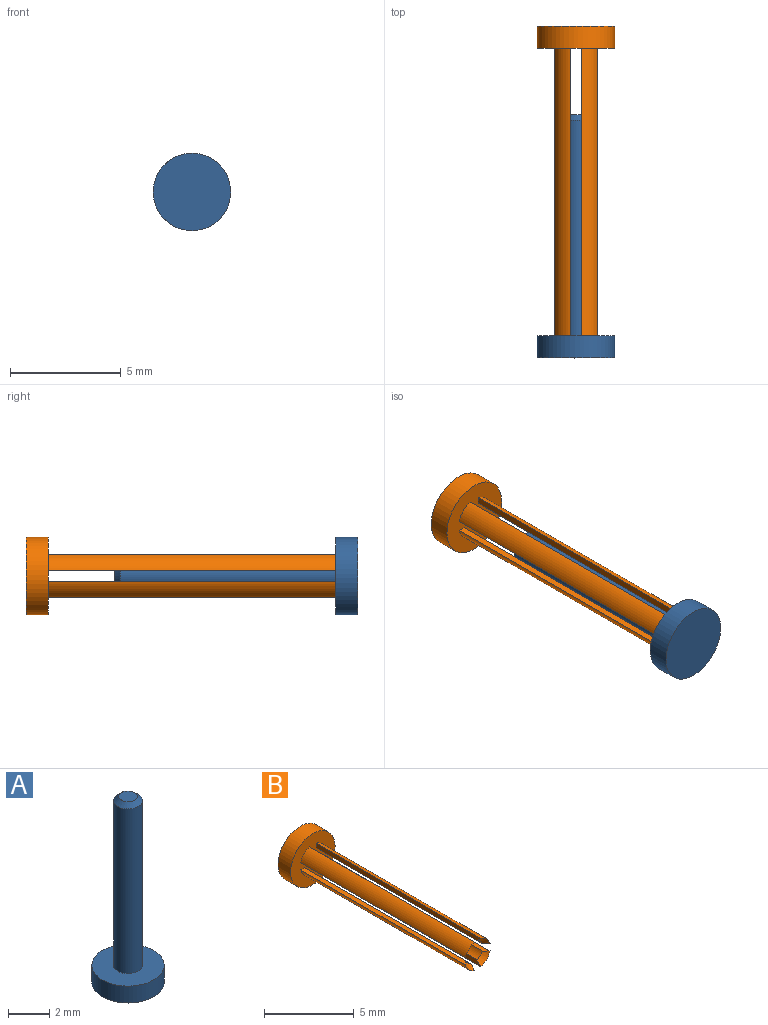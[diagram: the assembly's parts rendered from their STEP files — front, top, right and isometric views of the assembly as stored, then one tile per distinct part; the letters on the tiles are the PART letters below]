
ASSEMBLY  parts=2 mates=1
PART A: 6 faces, bbox 3.5x3.5x11 mm
  f0: cylinder r=1.75mm len=3.5mm, axis (0,0,-1), area 11mm2, adj f1,f2
  f1: plane 3.5x3.5mm, normal (0,0,1), area 8.1mm2, adj f0,f3
  f2: plane 3.5x3.5mm, normal (0,0,-1), area 9.6mm2, adj f0
  f3: cylinder r=0.7mm len=9.75mm, axis (0,0,-1), area 42.9mm2, adj f1,f5
  f4: plane 0.9x0.9mm, normal (0,0,1), area 0.6mm2, adj f5
  f5: cone r=0.45mm half-angle=45deg, axis (0,0,-1), area 1.3mm2, adj f3,f4
PART B: 23 faces, bbox 3.5x14x3.5 mm
  f0: cylinder r=1mm len=13mm, axis (0,1,0), area 13.9mm2, adj f7,f11,f17,f20
  f1: cylinder r=1mm len=13mm, axis (0,1,0), area 13.9mm2, adj f7,f16,f18,f21
  f2: cylinder r=1mm len=13mm, axis (0,1,0), area 13.9mm2, adj f7,f12,f13,f19
  f3: cylinder r=0.7mm len=12.7mm, axis (0,-1,0), area 7.5mm2, adj f7,f11,f17,f20
  f4: cylinder r=0.7mm len=12.7mm, axis (0,-1,0), area 7.5mm2, adj f7,f16,f18,f21
  f5: cylinder r=0.7mm len=12.7mm, axis (0,-1,0), area 7.5mm2, adj f7,f12,f13,f19
  f6: cylinder r=1.75mm len=3.5mm, axis (0,1,0), area 11mm2, adj f7,f8
  f7: plane 3.5x3.5mm, normal (0,-1,0), area 8.6mm2, adj f0,f1,f2,f3,f4,f5,f6,f9
  f8: plane 3.5x3.5mm, normal (0,1,0), area 9.6mm2, adj f6
  f9: cylinder r=1mm len=13mm, axis (0,1,0), area 13.9mm2, adj f7,f14,f15,f22
  f10: cylinder r=0.7mm len=12.7mm, axis (0,-1,0), area 7.5mm2, adj f7,f14,f15,f22
  f11: plane 13.02x0.33mm, normal (-1,0,0), area 4mm2, adj f0,f3,f7,f20
  f12: plane 13.02x0.33mm, normal (1,0,0), area 4mm2, adj f2,f5,f7,f19
  f13: plane 13.02x0.33mm, normal (0,0,1), area 4mm2, adj f2,f5,f7,f19
  f14: plane 13.02x0.33mm, normal (0,0,-1), area 4mm2, adj f7,f9,f10,f22
  f15: plane 13.02x0.33mm, normal (1,0,0), area 4mm2, adj f7,f9,f10,f22
  f16: plane 13.02x0.33mm, normal (-1,0,0), area 4mm2, adj f1,f4,f7,f21
  f17: plane 13.02x0.33mm, normal (0,0,1), area 4mm2, adj f0,f3,f7,f20
  f18: plane 13.02x0.33mm, normal (0,0,-1), area 4mm2, adj f1,f4,f7,f21
  f19: cone r=0.7mm half-angle=45deg, axis (0,-1,0), area 0.3mm2, adj f2,f5,f12,f13
  f20: cone r=0.7mm half-angle=45deg, axis (0,-1,0), area 0.3mm2, adj f0,f3,f11,f17
  f21: cone r=0.7mm half-angle=45deg, axis (0,-1,0), area 0.3mm2, adj f1,f4,f16,f18
  f22: cone r=0.7mm half-angle=45deg, axis (0,-1,0), area 0.3mm2, adj f9,f10,f14,f15
PLACE A rot(axis=(-1,0,0),90deg) t=(-2.49,-10.28,-1.26)mm
PLACE B t=(-2.49,4.72,-1.26)mm
MATE fastened A.f3 <-> B.f0  axis (0,-1,0) through (-2.49,-9.28,-1.26)mm
